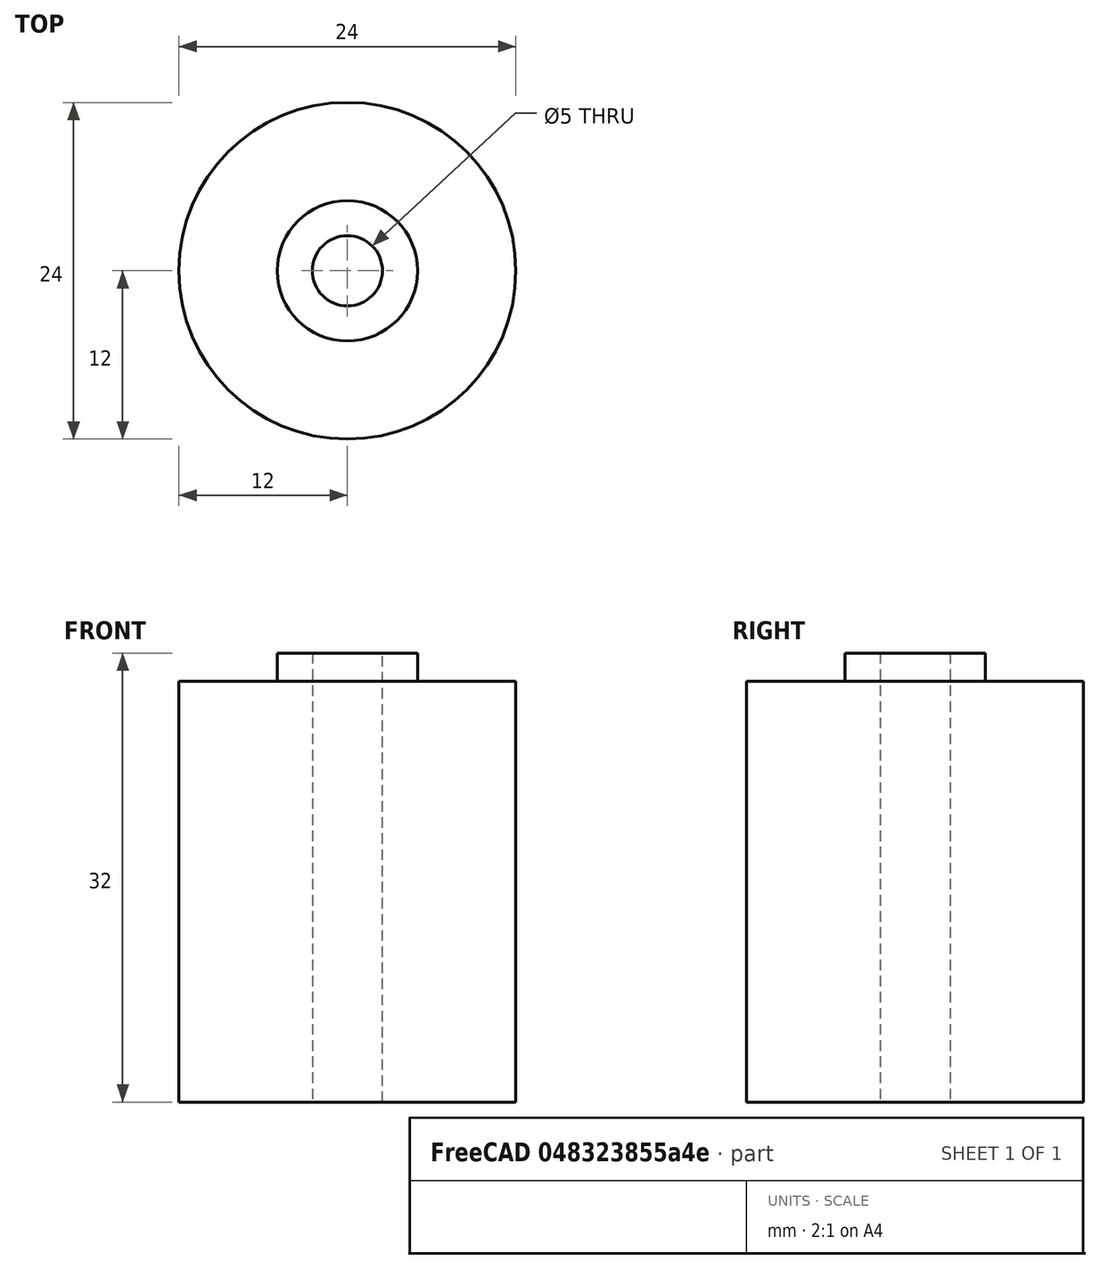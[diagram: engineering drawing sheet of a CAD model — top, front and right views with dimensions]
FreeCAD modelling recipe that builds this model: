
FCSTD DOCUMENT  (FreeCAD 1.0R39109 (Git))
Label: RGB-Ball-Fassung
License: All rights reserved
LicenseURL: https://en.wikipedia.org/wiki/All_rights_reserved
objects: Part::Cylinder×3, Measure::MeasureDistance×2, Part::MultiFuse×1, Part::Cut×1, Measure::MeasureRadius×1, App::DocumentObjectGroup×1
note: 5 computed .brp shape members not serialized (recipe doc carries the construction recipe); baked Part::Feature solids carry a one-line shape summary decoded from their .brp

FEATURE [Part::Cylinder] Cylinder
  Angle = 360
  AttacherType = Attacher::AttachEngine3D
  FirstAngle = 0
  Height = 30
  Radius = 12
  SecondAngle = 0
FEATURE [Part::Cylinder] Cylinder001
  Angle = 360
  AttacherType = Attacher::AttachEngine3D
  FirstAngle = 0
  Height = 2
  Placement = pos=(0,0,30) rot=(0,0,1;0rad)
  Radius = 5
  SecondAngle = 0
FEATURE [Part::Cylinder] Cylinder002
  Angle = 360
  AttacherType = Attacher::AttachEngine3D
  FirstAngle = 0
  Height = 40
  Placement = pos=(0,0,-2) rot=(0,0,1;0rad)
  Radius = 2.5
  SecondAngle = 0
FEATURE [Part::MultiFuse] Fusion
  Refine = true
  Shapes = -> [Cylinder,Cylinder001]
FEATURE [Part::Cut] Cut
  Base = -> Fusion
  Refine = true
  Tool = -> Cylinder002
FEATURE [Measure::MeasureDistance] Distance  label="Hoehe: 30,00 mm"
  Distance = 30
  DistanceX = 0
  DistanceY = 0
  DistanceZ = 30
  Element1 = -> Cut [Edge3]
  Element2 = -> Cut [Edge2]
  Position1 = (0,0,30)
  Position2 = (0,0,0)
FEATURE [Measure::MeasureRadius] Radius  label="Radius: 12,00 mm"
  Element = -> Cut [Edge3]
  Radius = 12
FEATURE [Measure::MeasureDistance] Distance001  label="Distance001: 2,00 mm"
  Distance = 2
  DistanceX = 0
  DistanceY = 0
  DistanceZ = 2
  Element1 = -> Cut [Edge9]
  Element2 = -> Cut [Edge5]
  Position1 = (0,0,32)
  Position2 = (0,0,30)
FEATURE [App::DocumentObjectGroup] Measurements
  Group = -> [Distance,Radius,Distance001]
